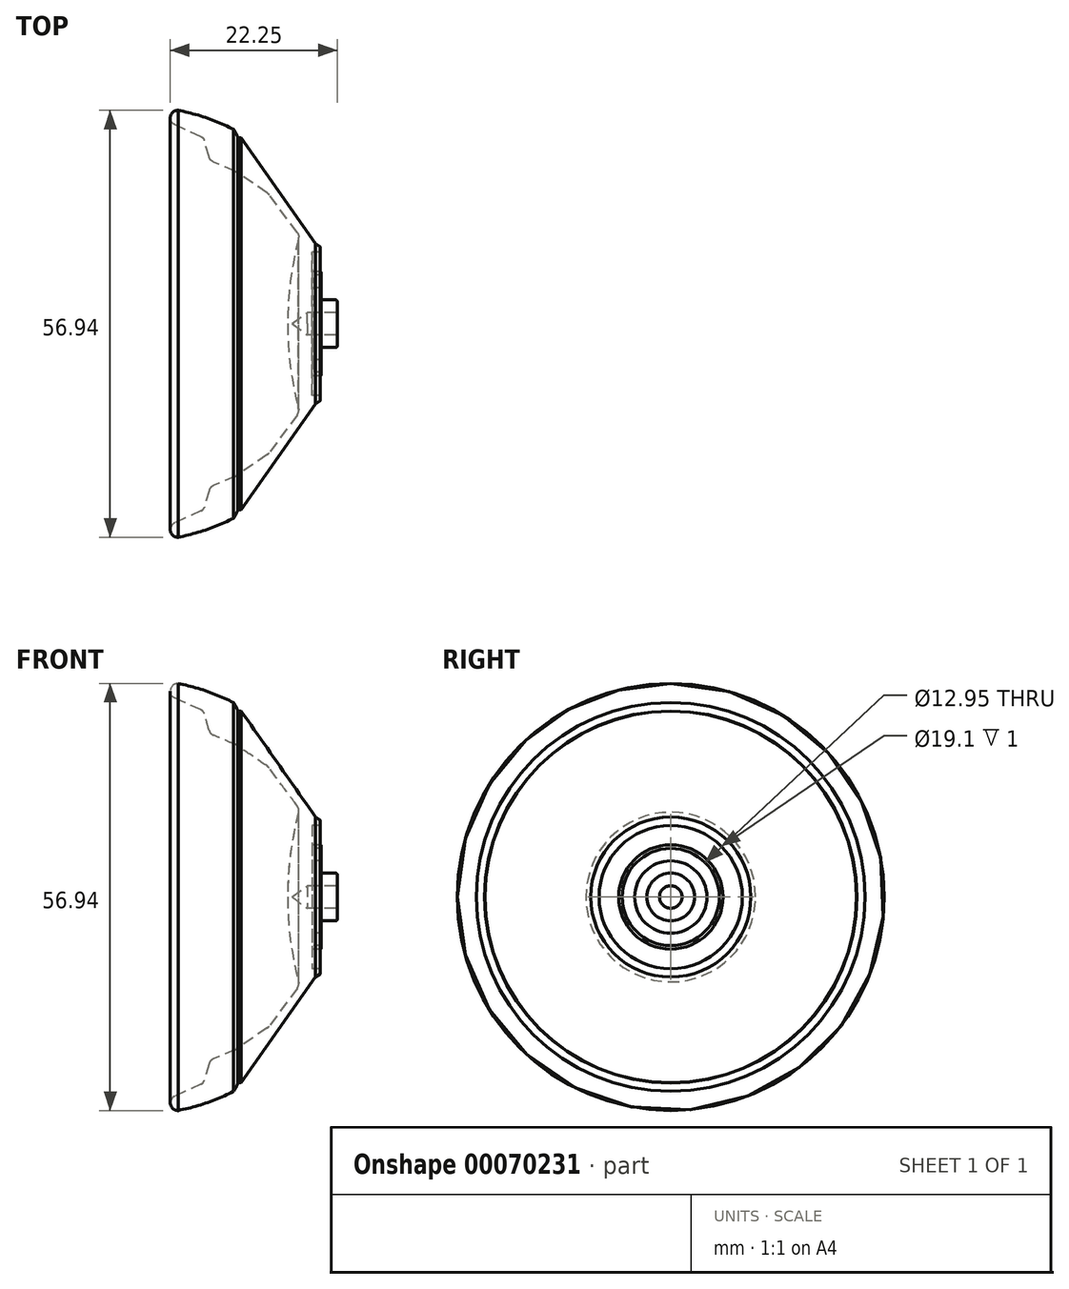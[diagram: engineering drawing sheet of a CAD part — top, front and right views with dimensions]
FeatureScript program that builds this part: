
annotation { "Feature Type Name" : "Feature", "Feature Type Description" : "" }
export const myFeature = defineFeature(function(context is Context, id is Id, definition is map)
    precondition{}
    {
        {
            var Q0;
            Q0=qCreatedBy(makeId("Front.planeOp"),FACE);
            var sketch = newSketch(context, id + "F0", { "sketchPlane" : qUnion([Q0])});
            skLineSegment(sketch, "E0", {"start": v(-27.14, 28.5) * mm, "end": v(36.68, 28.5) * mm, "construction": true});
            skLineSegment(sketch, "E1", {"start": v(20, 42.96) * mm, "end": v(20, -13.53) * mm, "construction": true});
            skLineSegment(sketch, "E2.bottom", {"start": v(22.05, 3.18) * mm, "end": v(20.1, 3.18) * mm});
            skLineSegment(sketch, "E2.left", {"start": v(22.25, 2.98) * mm, "end": v(22.25, 1.7) * mm});
            skLineSegment(sketch, "E3", {"start": v(20, 3.28) * mm, "end": v(20, 4.82) * mm});
            skLineSegment(sketch, "E4", {"start": v(20, 4.82) * mm, "end": v(19.3, 4.82) * mm});
            skLineSegment(sketch, "E5", {"start": v(19.2, 4.92) * mm, "end": v(19.2, 6.38) * mm});
            skLineSegment(sketch, "E6", {"start": v(19.3, 6.48) * mm, "end": v(20, 6.48) * mm});
            skLineSegment(sketch, "E7", {"start": v(20, 6.95) * mm, "end": v(18.9, 6.95) * mm});
            skLineSegment(sketch, "E8", {"start": v(18.9, 6.95) * mm, "end": v(18.9, 9.55) * mm});
            skLineSegment(sketch, "E9", {"start": v(18.9, 9.55) * mm, "end": v(19.9, 9.55) * mm});
            skLineSegment(sketch, "E10.top", {"start": v(20.1, 6.48) * mm, "end": v(20.1, 6.48) * mm});
            skLineSegment(sketch, "E10.left", {"start": v(20.1, 6.85) * mm, "end": v(20.1, 6.58) * mm});
            skLineSegment(sketch, "E11.right", {"start": v(20, 9.65) * mm, "end": v(20, 10.17) * mm});
            skPoint(sketch, "E12.visualSharp", {"position": v(20, 10.09) * mm});
            skArc(sketch, "E12.filletArc", {"start": v(20, 10.17) * mm, "mid": v(19.99, 10.22) * mm, "end": v(19.96, 10.25) * mm});
            skPoint(sketch, "E13.visualSharp", {"position": v(20, 9.55) * mm});
            skArc(sketch, "E13.filletArc", {"start": v(19.9, 9.55) * mm, "mid": v(19.97, 9.58) * mm, "end": v(20, 9.65) * mm});
            skPoint(sketch, "E14.visualSharp", {"position": v(20.1, 6.95) * mm});
            skArc(sketch, "E14.filletArc", {"start": v(20.1, 6.85) * mm, "mid": v(20.07, 6.92) * mm, "end": v(20, 6.95) * mm});
            skPoint(sketch, "E15.visualSharp", {"position": v(20.1, 6.48) * mm});
            skArc(sketch, "E15.filletArc", {"start": v(20, 6.48) * mm, "mid": v(20.07, 6.5) * mm, "end": v(20.1, 6.58) * mm});
            skPoint(sketch, "E16.visualSharp", {"position": v(19.2, 6.48) * mm});
            skArc(sketch, "E16.filletArc", {"start": v(19.3, 6.48) * mm, "mid": v(19.23, 6.45) * mm, "end": v(19.2, 6.38) * mm});
            skPoint(sketch, "E17.visualSharp", {"position": v(19.2, 4.82) * mm});
            skArc(sketch, "E17.filletArc", {"start": v(19.2, 4.92) * mm, "mid": v(19.23, 4.85) * mm, "end": v(19.3, 4.82) * mm});
            skPoint(sketch, "E18.visualSharp", {"position": v(20, 3.18) * mm});
            skArc(sketch, "E18.filletArc", {"start": v(20, 3.28) * mm, "mid": v(20.03, 3.2) * mm, "end": v(20.1, 3.18) * mm});
            skPoint(sketch, "E19.visualSharp", {"position": v(22.25, 3.18) * mm});
            skArc(sketch, "E19.filletArc", {"start": v(22.25, 2.98) * mm, "mid": v(22.2, 3.12) * mm, "end": v(22.05, 3.17) * mm});
            skLineSegment(sketch, "E20", {"start": v(22.05, 1.5) * mm, "end": v(18.25, 1.5) * mm});
            skPoint(sketch, "E21.visualSharp", {"position": v(22.25, 1.5) * mm});
            skArc(sketch, "E21.filletArc", {"start": v(22.05, 1.5) * mm, "mid": v(22.2, 1.56) * mm, "end": v(22.25, 1.7) * mm});
            skLineSegment(sketch, "E22", {"start": v(0.59, 26.55) * mm, "end": v(4.1, 24.95) * mm});
            skLineSegment(sketch, "E23", {"start": v(4.53, 24.46) * mm, "end": v(5.17, 22.23) * mm});
            skLineSegment(sketch, "E24", {"start": v(5.74, 21.58) * mm, "end": v(8.64, 20.35) * mm});
            skLineSegment(sketch, "E25", {"start": v(8.8, 20.25) * mm, "end": v(12.92, 17.46) * mm});
            skLineSegment(sketch, "E26", {"start": v(13.16, 17.23) * mm, "end": v(16.92, 12.15) * mm});
            skLineSegment(sketch, "E27", {"start": v(15.65, 0) * mm, "end": v(16.2, 0) * mm});
            skLineSegment(sketch, "E28", {"start": v(16.2, 0) * mm, "end": v(18.25, 1.5) * mm});
            skPoint(sketch, "E29.visualSharp", {"position": v(0, 28.5) * mm});
            skPoint(sketch, "E30.visualSharp", {"position": v(-13.41, 32.9) * mm});
            skArc(sketch, "E30.filletArc", {"start": v(1.06, 28.46) * mm, "mid": v(0.03, 27.7) * mm, "end": v(0.59, 26.55) * mm});
            skLineSegment(sketch, "E31", {"start": v(19.37, 10.67) * mm, "end": v(19.96, 10.25) * mm});
            skPoint(sketch, "E32.visualSharp", {"position": v(4.44, 24.8) * mm});
            skArc(sketch, "E32.filletArc", {"start": v(4.53, 24.46) * mm, "mid": v(4.38, 24.75) * mm, "end": v(4.1, 24.95) * mm});
            skPoint(sketch, "E33.visualSharp", {"position": v(5.3, 21.77) * mm});
            skArc(sketch, "E33.filletArc", {"start": v(5.17, 22.23) * mm, "mid": v(5.38, 21.84) * mm, "end": v(5.74, 21.58) * mm});
            skPoint(sketch, "E34.visualSharp", {"position": v(8.73, 20.3) * mm});
            skArc(sketch, "E34.filletArc", {"start": v(8.8, 20.25) * mm, "mid": v(8.72, 20.3) * mm, "end": v(8.64, 20.35) * mm});
            skLineSegment(sketch, "E35", {"start": v(9.45, 24.77) * mm, "end": v(19.37, 10.67) * mm});
            skArc(sketch, "E36.filletArc", {"start": v(17.09, 11.31) * mm, "mid": v(17.1, 11.75) * mm, "end": v(16.92, 12.15) * mm});
            skPoint(sketch, "E37.visualSharp", {"position": v(13.06, 17.36) * mm});
            skArc(sketch, "E37.filletArc", {"start": v(13.16, 17.23) * mm, "mid": v(13.05, 17.35) * mm, "end": v(12.92, 17.46) * mm});
            skArc(sketch, "E38", {"start": v(17.09, 11.31) * mm, "mid": v(16, 5.7) * mm, "end": v(15.65, 0) * mm});
            skArc(sketch, "E39", {"start": v(9.03, 24.81) * mm, "mid": v(8.76, 25.38) * mm, "end": v(8.44, 25.92) * mm});
            skArc(sketch, "E40", {"start": v(8.44, 25.92) * mm, "mid": v(4.84, 27.45) * mm, "end": v(1.06, 28.46) * mm});
            skLineSegment(sketch, "E41", {"start": v(9.45, 24.77) * mm, "end": v(9.03, 24.81) * mm});
            skSolve(sketch);
        }
        {
            var Q0;
            Q0=makeQuery(id+"F0.imprint","IMPRINT",FACE,{"disambiguationData":[TD([[makeQuery(id+"F0.imprint","IMPRINT",EDGE,{"derivedFrom":sQuery(id+"F0.wireOp",EDGE,"E2.bottom")}),1.0]])]});
            var Q1;
            Q1=sQuery(id+"F0.wireOp",EDGE,"E27");
            revolve(context, id + "F1", {"entities" : qUnion([Q0]), "axis" : qUnion([Q1]), "revolveType" : RevolveType.FULL});
        }
    });
